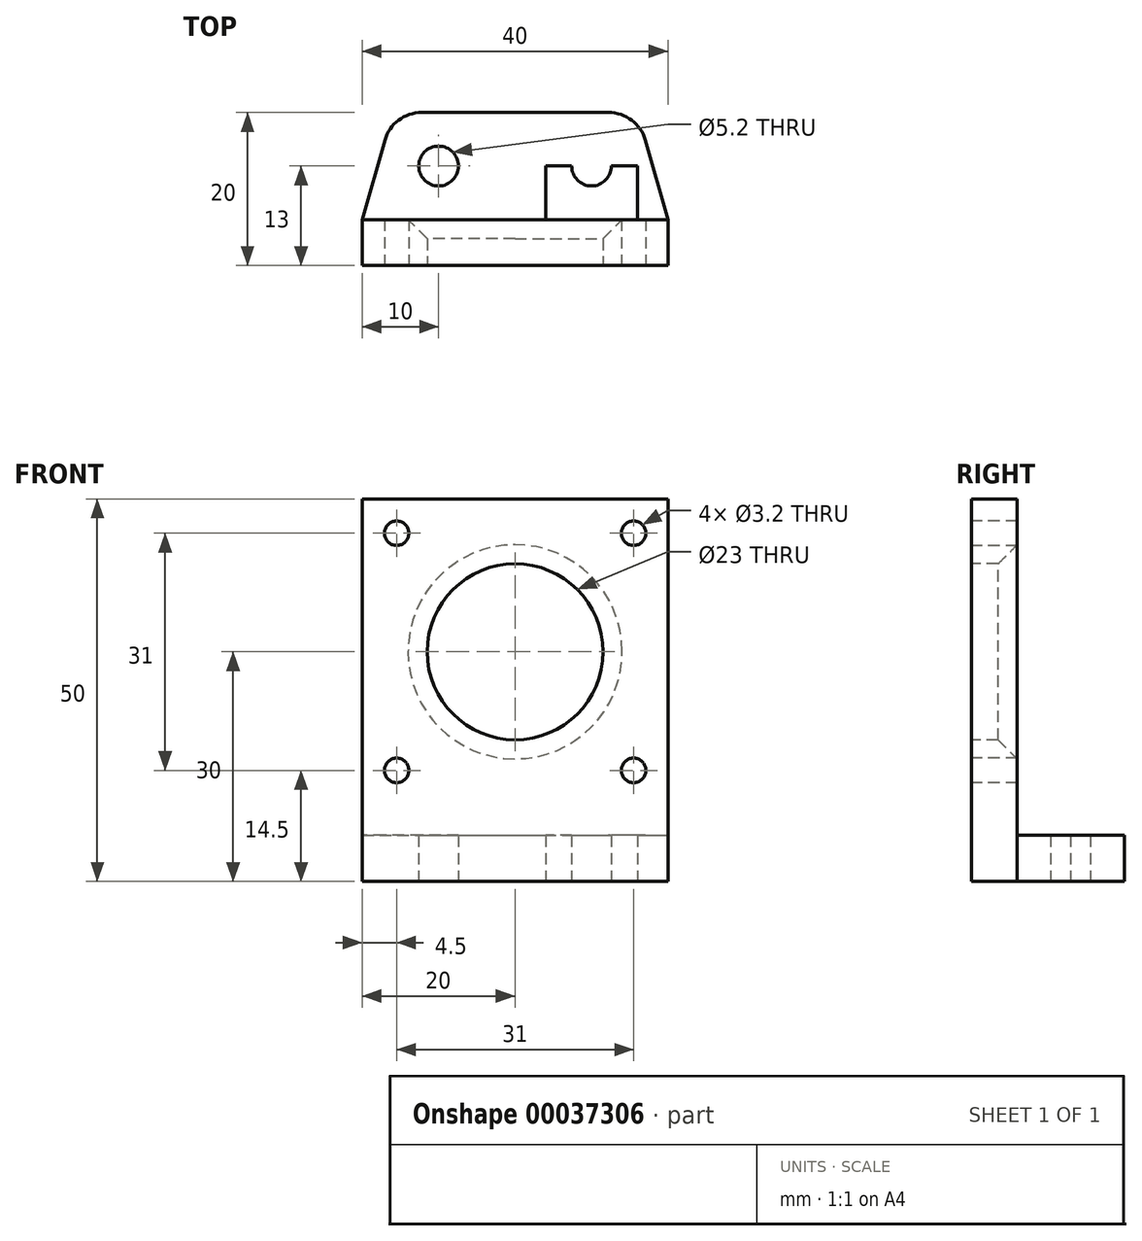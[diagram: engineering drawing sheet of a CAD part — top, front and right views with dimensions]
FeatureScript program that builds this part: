
annotation { "Feature Type Name" : "Feature", "Feature Type Description" : "" }
export const myFeature = defineFeature(function(context is Context, id is Id, definition is map)
    precondition{}
    {
        {
            assignVariable(context, id + "F0", {"name" : "defaultThickness", "anyValue" : 6 * mm});
        }
        {
            var Q0;
            Q0=qCreatedBy(makeId("Top.planeOp"),FACE);
            var sketch = newSketch(context, id + "F1", { "sketchPlane" : qUnion([Q0])});
            skLineSegment(sketch, "E0.rect.bottom", {"start": v(-20, 17.5) * mm, "end": v(20, 17.5) * mm});
            skLineSegment(sketch, "E0.rect.top", {"start": v(-20, 23.5) * mm, "end": v(20, 23.5) * mm});
            skLineSegment(sketch, "E0.rect.left", {"start": v(-20, 17.5) * mm, "end": v(-20, 23.5) * mm});
            skLineSegment(sketch, "E0.rect.right", {"start": v(20, 17.5) * mm, "end": v(20, 23.5) * mm});
            skPoint(sketch, "E0.rect.middle", {"position": v(0, 20.5) * mm});
            skLineSegment(sketch, "E1", {"start": v(-16, 23.5) * mm, "end": v(-16, 37.5) * mm});
            skLineSegment(sketch, "E2", {"start": v(-16, 37.5) * mm, "end": v(-4, 37.5) * mm});
            skLineSegment(sketch, "E3", {"start": v(-4, 37.5) * mm, "end": v(-4, 23.5) * mm});
            skLineSegment(sketch, "E4", {"start": v(-10, 37.5) * mm, "end": v(-10, 23.5) * mm, "construction": true});
            skLineSegment(sketch, "E5", {"start": v(-16, 30.5) * mm, "end": v(-4, 30.5) * mm, "construction": true});
            skPoint(sketch, "E6", {"position": v(-10, 30.5) * mm});
            skLineSegment(sketch, "E7", {"start": v(-16, 23.5) * mm, "end": v(-4, 23.5) * mm});
            skCircle(sketch, "E8", {"center": v(-10, 30.5) * mm, "radius": 2.6 * mm});
            skLineSegment(sketch, "E9.MirrorCS", {"start": v(16, 23.5) * mm, "end": v(4, 23.5) * mm});
            skPoint(sketch, "E10.MirrorP", {"position": v(10, 30.5) * mm});
            skLineSegment(sketch, "E11.MirrorCS", {"start": v(10, 37.5) * mm, "end": v(10, 23.5) * mm});
            skLineSegment(sketch, "E12.MirrorCS", {"start": v(16, 30.5) * mm, "end": v(4, 30.5) * mm});
            skCircle(sketch, "E13.MirrorC", {"center": v(10, 30.5) * mm, "radius": 2.6 * mm});
            skLineSegment(sketch, "E14.MirrorCS", {"start": v(4, 37.5) * mm, "end": v(4, 23.5) * mm});
            skLineSegment(sketch, "E15.MirrorCS", {"start": v(16, 37.5) * mm, "end": v(4, 37.5) * mm});
            skLineSegment(sketch, "E16.MirrorCS", {"start": v(16, 23.5) * mm, "end": v(16, 37.5) * mm});
            skLineSegment(sketch, "E17", {"start": v(-16, 37.5) * mm, "end": v(-20, 23.5) * mm});
            skLineSegment(sketch, "E18", {"start": v(16, 37.5) * mm, "end": v(20, 23.5) * mm});
            skLineSegment(sketch, "E19", {"start": v(-4, 37.5) * mm, "end": v(4, 37.5) * mm});
            skSolve(sketch);
        }
        {
            var Q0;
            Q0=makeQuery(id+"F1.imprint","IMPRINT",FACE,{"disambiguationData":[TD([[makeQuery(id+"F1.imprint","IMPRINT",EDGE,{"derivedFrom":sQuery(id+"F1.wireOp",EDGE,"E1")}),-1.0]])]});
            var Q1;
            {var subQ0=sQuery(id+"F1.wireOp",EDGE,"E15.MirrorCS");var subQ3=sQuery(id+"F1.wireOp",EDGE,"E11.MirrorCS");var subQ4=makeQuery(id+"F1.imprint","INTERSECT",VERTEX,{"derivedFrom":[subQ3,subQ0]});Q1=makeQuery(id+"F1.imprint","IMPRINT",FACE,{"disambiguationData":[TD([[makeQuery(id+"F1.imprint","IMPRINT",EDGE,{"disambiguationData":[TD([[subQ4,-1.0]])],"derivedFrom":subQ3}),-1.0]])]});}
            var Q2;
            {var subQ1=sQuery(id+"F1.wireOp",EDGE,"E15.MirrorCS");var subQ5=sQuery(id+"F1.wireOp",EDGE,"E11.MirrorCS");var subQ6=makeQuery(id+"F1.imprint","INTERSECT",VERTEX,{"derivedFrom":[subQ5,subQ1]});Q2=makeQuery(id+"F1.imprint","IMPRINT",FACE,{"disambiguationData":[TD([[makeQuery(id+"F1.imprint","IMPRINT",EDGE,{"disambiguationData":[TD([[subQ6,-1.0]])],"derivedFrom":subQ5}),1.0]])]});}
            var Q3;
            {var subQ3=sQuery(id+"F1.wireOp",EDGE,"E9.MirrorCS");var subQ7=sQuery(id+"F1.wireOp",EDGE,"E11.MirrorCS");var subQ9=makeQuery(id+"F1.imprint","INTERSECT",VERTEX,{"derivedFrom":[subQ3,subQ7]});Q3=makeQuery(id+"F1.imprint","IMPRINT",FACE,{"disambiguationData":[TD([[makeQuery(id+"F1.imprint","IMPRINT",EDGE,{"disambiguationData":[TD([[subQ9,1.0]])],"derivedFrom":subQ7}),1.0]])]});}
            var Q4;
            {var subQ3=sQuery(id+"F1.wireOp",EDGE,"E9.MirrorCS");var subQ7=sQuery(id+"F1.wireOp",EDGE,"E11.MirrorCS");var subQ9=makeQuery(id+"F1.imprint","INTERSECT",VERTEX,{"derivedFrom":[subQ3,subQ7]});Q4=makeQuery(id+"F1.imprint","IMPRINT",FACE,{"disambiguationData":[TD([[makeQuery(id+"F1.imprint","IMPRINT",EDGE,{"disambiguationData":[TD([[subQ9,1.0]])],"derivedFrom":subQ7}),-1.0]])]});}
            var Q5;
            {var subQ1=sQuery(id+"F1.wireOp",EDGE,"E1");Q5=makeQuery(id+"F1.imprint","IMPRINT",FACE,{"disambiguationData":[TD([[makeQuery(id+"F1.imprint","IMPRINT",EDGE,{"derivedFrom":subQ1}),1.0]])]});}
            var Q6;
            {var subQ5=sQuery(id+"F1.wireOp",EDGE,"E3");Q6=makeQuery(id+"F1.imprint","IMPRINT",FACE,{"disambiguationData":[TD([[makeQuery(id+"F1.imprint","IMPRINT",EDGE,{"derivedFrom":subQ5}),1.0]])]});}
            var Q7;
            {var subQ0=sQuery(id+"F1.wireOp",EDGE,"E18");Q7=makeQuery(id+"F1.imprint","IMPRINT",FACE,{"disambiguationData":[TD([[makeQuery(id+"F1.imprint","IMPRINT",EDGE,{"derivedFrom":subQ0}),-1.0]])]});}
            extrude(context, id + "F2", {"entities" : qUnion([Q0, Q1, Q2, Q3, Q4, Q5, Q6, Q7]), "depth" : getVariable(context, 'defaultThickness')});
        }
        {
            var Q0;
            Q0=makeQuery(id+"F1.imprint","IMPRINT",FACE,{"disambiguationData":[TD([[makeQuery(id+"F1.imprint","IMPRINT",EDGE,{"derivedFrom":sQuery(id+"F1.wireOp",EDGE,"E0.rect.bottom")}),1.0]])]});
            extrude(context, id + "F3", {"entities" : qUnion([Q0]), "depth" : 50 * mm});
        }
        {
            var Q0;
            Q0=makeQuery(id+"F3.opExtrude","SWEPT_FACE",FACE,{"disambiguationData":[OSD([sQuery(id+"F1.wireOp",EDGE,"E0.rect.bottom")])]});
            var sketch = newSketch(context, id + "F4", { "sketchPlane" : qUnion([Q0])});
            skLineSegment(sketch, "E20", {"start": v(0, 50) * mm, "end": v(0, 0) * mm, "construction": true});
            skLineSegment(sketch, "E21", {"start": v(-20, 30) * mm, "end": v(20, 30) * mm, "construction": true});
            skCircle(sketch, "E22", {"center": v(0, 30) * mm, "radius": 11.5 * mm});
            skCircle(sketch, "E23", {"center": v(-15.5, 45.5) * mm, "radius": 1.6 * mm});
            skCircle(sketch, "E24", {"center": v(-15.5, 14.5) * mm, "radius": 1.6 * mm});
            skCircle(sketch, "E25", {"center": v(15.5, 14.5) * mm, "radius": 1.6 * mm});
            skCircle(sketch, "E26", {"center": v(15.5, 45.5) * mm, "radius": 1.6 * mm});
            skSolve(sketch);
        }
        {
            var Q0;
            Q0=qSketchRegion(id+"F4",true);
            extrude(context, id + "F5", {"entities" : qUnion([Q0]), "operationType" : NewBodyOperationType.REMOVE, "endBound" : BoundingType.THROUGH_ALL, "oppositeDirection" : true, "depth" : 25 * mm});
        }
        {
            var Q0;
            Q0=makeQuery(id+"F6.opExtrude","SWEPT_EDGE",EDGE,{"disambiguationData":[OSD([sQuery(id+"FPKVRYglfgyGCyF_1.wireOp",EDGE,"306b3cfc-551d-497d-8c43-a8ed09669cc44.MirrorCS"),sQuery(id+"FPKVRYglfgyGCyF_1.wireOp",EDGE,"306b3cfc-551d-497d-8c43-a8ed09669cc45.MirrorCS"),sQuery(id+"FPKVRYglfgyGCyF_1.wireOp",EDGE,"306b3cfc-551d-497d-8c43-a8ed09669cc410.MirrorCS")])]});
            var Q1;
            Q1=makeQuery(id+"F6.opExtrude","SWEPT_EDGE",EDGE,{"disambiguationData":[OSD([sQuery(id+"FPKVRYglfgyGCyF_1.wireOp",EDGE,"306b3cfc-551d-497d-8c43-a8ed09669cc46.MirrorCS"),sQuery(id+"FPKVRYglfgyGCyF_1.wireOp",EDGE,"306b3cfc-551d-497d-8c43-a8ed09669cc47.MirrorCS"),sQuery(id+"FPKVRYglfgyGCyF_1.wireOp",EDGE,"306b3cfc-551d-497d-8c43-a8ed09669cc410.MirrorCS")])]});
            var Q2;
            Q2=makeQuery(id+"F6.opExtrude","SWEPT_EDGE",EDGE,{"disambiguationData":[OSD([sQuery(id+"FPKVRYglfgyGCyF_1.wireOp",EDGE,"a75c6c92-6b33-47ab-839a-70fd0e169de0"),sQuery(id+"FPKVRYglfgyGCyF_1.wireOp",EDGE,"e9842276-5117-4aed-8551-042d3347c8a4"),sQuery(id+"FPKVRYglfgyGCyF_1.wireOp",EDGE,"1b59d14f-a3ec-4578-90db-0e0e2cb720d3")])]});
            var Q3;
            Q3=makeQuery(id+"F6.opExtrude","SWEPT_EDGE",EDGE,{"disambiguationData":[OSD([sQuery(id+"FPKVRYglfgyGCyF_1.wireOp",EDGE,"e1829bb6-4c8f-4a3e-b7cc-f9a1525636db"),sQuery(id+"FPKVRYglfgyGCyF_1.wireOp",EDGE,"a75c6c92-6b33-47ab-839a-70fd0e169de0"),sQuery(id+"FPKVRYglfgyGCyF_1.wireOp",EDGE,"f6659a32-1e39-4f74-95a5-c9b4f418ae41")])]});
            var Q4;
            Q4=makeQuery(id+"F2.opExtrude","SWEPT_EDGE",EDGE,{"disambiguationData":[OSD([sQuery(id+"F1.wireOp",EDGE,"E15.MirrorCS"),sQuery(id+"F1.wireOp",EDGE,"E16.MirrorCS"),sQuery(id+"F1.wireOp",EDGE,"E18")])]});
            var Q5;
            Q5=makeQuery(id+"F2.opExtrude","SWEPT_EDGE",EDGE,{"disambiguationData":[OSD([sQuery(id+"F1.wireOp",EDGE,"E1"),sQuery(id+"F1.wireOp",EDGE,"E2"),sQuery(id+"F1.wireOp",EDGE,"E17")])]});
            fillet(context, id + "F7", {"entities" : qUnion([Q0, Q1, Q2, Q3, Q4, Q5]), "radius" : 5 * mm, "tangentPropagation" : true, "allowEdgeOverflow" : false});
        }
        {
            var Q0;
            Q0=makeQuery(id+"F5.boolean.opBoolean","INTERSECT",EDGE,{"derivedFrom":[makeQuery(id+"F3.opExtrude","SWEPT_FACE",FACE,{"disambiguationData":[OSD([sQuery(id+"F1.wireOp",EDGE,"E0.rect.top"),sQuery(id+"F1.wireOp",EDGE,"E7"),sQuery(id+"F1.wireOp",EDGE,"E9.MirrorCS")])]}),makeQuery(id+"F5.opExtrude","SWEPT_FACE",FACE,{"disambiguationData":[OSD([sQuery(id+"F4.wireOp",EDGE,"E22")])]})]});
            chamfer(context, id + "F8", {"entities" : qUnion([Q0]), "width" : 2.5 * mm, "tangentPropagation" : true});
        }
    });
